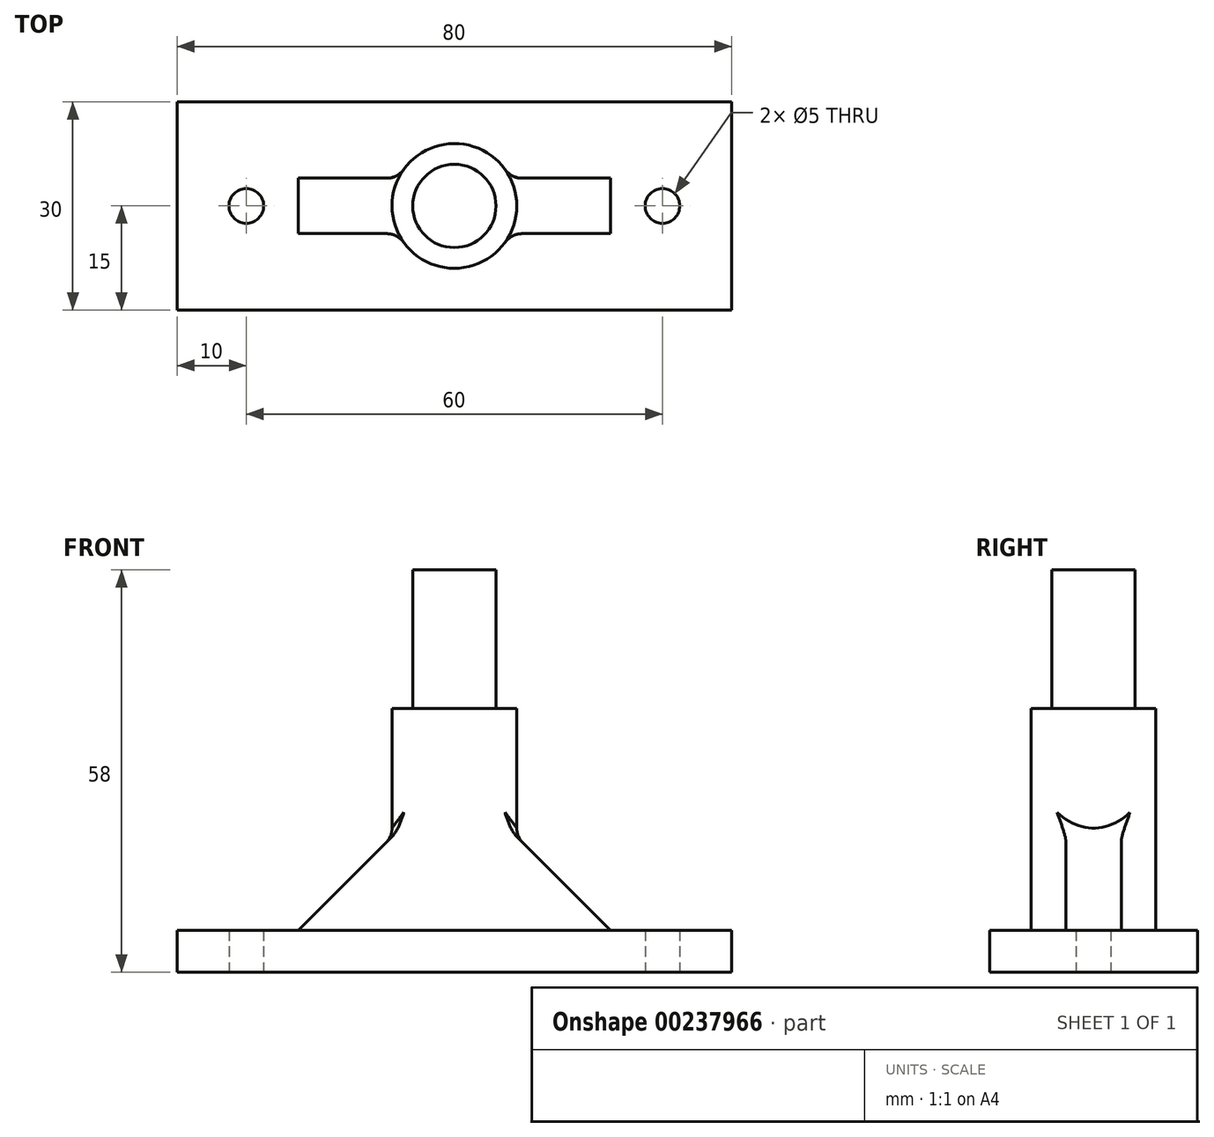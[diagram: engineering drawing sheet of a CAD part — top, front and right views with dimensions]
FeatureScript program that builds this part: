
annotation { "Feature Type Name" : "Feature", "Feature Type Description" : "" }
export const myFeature = defineFeature(function(context is Context, id is Id, definition is map)
    precondition{}
    {
        {
            var Q0;
            Q0=qCreatedBy(makeId("Top.planeOp"),FACE);
            var sketch = newSketch(context, id + "F0", { "sketchPlane" : qUnion([Q0])});
            skLineSegment(sketch, "E0.bottom", {"start": v(-40, 15) * mm, "end": v(40, 15) * mm});
            skLineSegment(sketch, "E0.top", {"start": v(-40, -15) * mm, "end": v(40, -15) * mm});
            skLineSegment(sketch, "E0.left", {"start": v(-40, 15) * mm, "end": v(-40, -15) * mm});
            skLineSegment(sketch, "E0.right", {"start": v(40, 15) * mm, "end": v(40, -15) * mm});
            skCircle(sketch, "E1", {"center": v(-30, 0) * mm, "radius": 2.5 * mm});
            skCircle(sketch, "E2", {"center": v(30, 0) * mm, "radius": 2.5 * mm});
            skSolve(sketch);
        }
        {
            var Q0;
            Q0=makeQuery(id+"F0.imprint","IMPRINT",FACE,{"disambiguationData":[TD([[makeQuery(id+"F0.imprint","IMPRINT",EDGE,{"derivedFrom":sQuery(id+"F0.wireOp",EDGE,"E0.bottom")}),-1.0]])]});
            extrude(context, id + "F1", {"entities" : qUnion([Q0]), "depth" : 6 * mm});
        }
        {
            var Q0;
            Q0=makeQuery(id+"F1.opExtrude","CAP_FACE",FACE,{"disambiguationData":[OSD([sQuery(id+"F0.wireOp",EDGE,"E0.bottom"),sQuery(id+"F0.wireOp",EDGE,"E0.top"),sQuery(id+"F0.wireOp",EDGE,"E0.left"),sQuery(id+"F0.wireOp",EDGE,"E0.right"),sQuery(id+"F0.wireOp",EDGE,"E1"),sQuery(id+"F0.wireOp",EDGE,"E2")])],"isStart":false});
            var sketch = newSketch(context, id + "F2", { "sketchPlane" : qUnion([Q0])});
            skCircle(sketch, "E3", {"center": v(0, 0) * mm, "radius": 9 * mm});
            skSolve(sketch);
        }
        {
            var Q0;
            Q0=makeQuery(id+"F2.imprint","IMPRINT",FACE,{"disambiguationData":[TD([[makeQuery(id+"F2.imprint","IMPRINT",EDGE,{"derivedFrom":sQuery(id+"F2.wireOp",EDGE,"E3")}),1.0]])]});
            extrude(context, id + "F3", {"entities" : qUnion([Q0]), "operationType" : NewBodyOperationType.ADD, "depth" : 32 * mm});
        }
        {
            var Q0;
            Q0=qCreatedBy(makeId("Front.planeOp"),FACE);
            var sketch = newSketch(context, id + "F4", { "sketchPlane" : qUnion([Q0])});
            skLineSegment(sketch, "E4", {"start": v(-7.5, 21) * mm, "end": v(-7.5, 6) * mm});
            skLineSegment(sketch, "E5", {"start": v(-7.5, 6) * mm, "end": v(-22.5, 6) * mm});
            skLineSegment(sketch, "E6", {"start": v(-22.5, 6) * mm, "end": v(-7.5, 21) * mm});
            skLineSegment(sketch, "E7", {"start": v(7.5, 21) * mm, "end": v(22.5, 6) * mm});
            skLineSegment(sketch, "E8", {"start": v(22.5, 6) * mm, "end": v(7.5, 6) * mm});
            skLineSegment(sketch, "E9", {"start": v(7.5, 6) * mm, "end": v(7.5, 21) * mm});
            skSolve(sketch);
        }
        {
            var Q0;
            Q0=makeQuery(id+"F4.imprint","IMPRINT",FACE,{"disambiguationData":[TD([[makeQuery(id+"F4.imprint","IMPRINT",EDGE,{"derivedFrom":sQuery(id+"F4.wireOp",EDGE,"E7")}),-1.0]])]});
            var Q1;
            Q1=makeQuery(id+"F4.imprint","IMPRINT",FACE,{"disambiguationData":[TD([[makeQuery(id+"F4.imprint","IMPRINT",EDGE,{"derivedFrom":sQuery(id+"F4.wireOp",EDGE,"E4")}),-1.0]])]});
            extrude(context, id + "F5", {"entities" : qUnion([Q0, Q1]), "operationType" : NewBodyOperationType.ADD, "endBound" : BoundingType.SYMMETRIC, "depth" : 8 * mm});
        }
        {
            var Q0;
            Q0=makeQuery(id+"F5.boolean.opBoolean","INTERSECT",EDGE,{"derivedFrom":[makeQuery(id+"F3.opExtrude","SWEPT_FACE",FACE,{"disambiguationData":[OSD([sQuery(id+"F2.wireOp",EDGE,"E3")])]}),makeQuery(id+"F5.opExtrude","SWEPT_FACE",FACE,{"disambiguationData":[OSD([sQuery(id+"F4.wireOp",EDGE,"E7")])]})]});
            var Q1;
            Q1=makeQuery(id+"F5.boolean.opBoolean","INTERSECT",EDGE,{"derivedFrom":[makeQuery(id+"F3.opExtrude","SWEPT_FACE",FACE,{"disambiguationData":[OSD([sQuery(id+"F2.wireOp",EDGE,"E3")])]}),makeQuery(id+"F5.opExtrude","SWEPT_FACE",FACE,{"disambiguationData":[OSD([sQuery(id+"F4.wireOp",EDGE,"E6")])]})]});
            var Q2;
            Q2=makeQuery(id+"F5.boolean.opBoolean","INTERSECT",EDGE,{"derivedFrom":[makeQuery(id+"F3.opExtrude","SWEPT_FACE",FACE,{"disambiguationData":[OSD([sQuery(id+"F2.wireOp",EDGE,"E3")])]}),makeQuery(id+"F5.opExtrude","CAP_FACE",FACE,{"disambiguationData":[OSD([sQuery(id+"F4.wireOp",EDGE,"E4"),sQuery(id+"F4.wireOp",EDGE,"E5"),sQuery(id+"F4.wireOp",EDGE,"E6")])],"isStart":false})]});
            var Q3;
            Q3=makeQuery(id+"F5.opExtrude","CAP_EDGE",EDGE,{"disambiguationData":[OSD([sQuery(id+"F4.wireOp",EDGE,"E5")])],"isStart":false});
            var Q4;
            Q4=makeQuery(id+"F5.boolean.opBoolean","INTERSECT",EDGE,{"derivedFrom":[makeQuery(id+"F3.opExtrude","SWEPT_FACE",FACE,{"disambiguationData":[OSD([sQuery(id+"F2.wireOp",EDGE,"E3")])]}),makeQuery(id+"F5.opExtrude","CAP_FACE",FACE,{"disambiguationData":[OSD([sQuery(id+"F4.wireOp",EDGE,"E7"),sQuery(id+"F4.wireOp",EDGE,"E8"),sQuery(id+"F4.wireOp",EDGE,"E9")])],"isStart":false})]});
            var Q5;
            Q5=makeQuery(id+"F5.opExtrude","CAP_EDGE",EDGE,{"disambiguationData":[OSD([sQuery(id+"F4.wireOp",EDGE,"E8")])],"isStart":false});
            var Q6;
            Q6=makeQuery(id+"F5.boolean.opBoolean","INTERSECT",EDGE,{"derivedFrom":[makeQuery(id+"F3.opExtrude","SWEPT_FACE",FACE,{"disambiguationData":[OSD([sQuery(id+"F2.wireOp",EDGE,"E3")])]}),makeQuery(id+"F5.opExtrude","CAP_FACE",FACE,{"disambiguationData":[OSD([sQuery(id+"F4.wireOp",EDGE,"E7"),sQuery(id+"F4.wireOp",EDGE,"E8"),sQuery(id+"F4.wireOp",EDGE,"E9")])],"isStart":true})]});
            var Q7;
            Q7=makeQuery(id+"F5.opExtrude","CAP_EDGE",EDGE,{"disambiguationData":[OSD([sQuery(id+"F4.wireOp",EDGE,"E8")])],"isStart":true});
            var Q8;
            Q8=makeQuery(id+"F5.opExtrude","SWEPT_EDGE",EDGE,{"disambiguationData":[OSD([sQuery(id+"F4.wireOp",EDGE,"E7"),sQuery(id+"F4.wireOp",EDGE,"E8")])]});
            var Q9;
            Q9=makeQuery(id+"F5.boolean.opBoolean","INTERSECT",EDGE,{"derivedFrom":[makeQuery(id+"F3.opExtrude","SWEPT_FACE",FACE,{"disambiguationData":[OSD([sQuery(id+"F2.wireOp",EDGE,"E3")])]}),makeQuery(id+"F5.opExtrude","CAP_FACE",FACE,{"disambiguationData":[OSD([sQuery(id+"F4.wireOp",EDGE,"E4"),sQuery(id+"F4.wireOp",EDGE,"E5"),sQuery(id+"F4.wireOp",EDGE,"E6")])],"isStart":true})]});
            var Q10;
            Q10=makeQuery(id+"F5.opExtrude","CAP_EDGE",EDGE,{"disambiguationData":[OSD([sQuery(id+"F4.wireOp",EDGE,"E5")])],"isStart":true});
            var Q11;
            Q11=makeQuery(id+"F5.opExtrude","SWEPT_EDGE",EDGE,{"disambiguationData":[OSD([sQuery(id+"F4.wireOp",EDGE,"E5"),sQuery(id+"F4.wireOp",EDGE,"E6")])]});
            fillet(context, id + "F6", {"entities" : qUnion([Q0, Q1, Q2, Q3, Q4, Q5, Q6, Q7, Q8, Q9, Q10, Q11]), "radius" : 3 * mm, "tangentPropagation" : true, "allowEdgeOverflow" : false});
        }
        {
            var Q0;
            Q0=makeQuery(id+"F3.opExtrude","CAP_FACE",FACE,{"disambiguationData":[OSD([sQuery(id+"F2.wireOp",EDGE,"E3")])],"isStart":false});
            var sketch = newSketch(context, id + "F7", { "sketchPlane" : qUnion([Q0])});
            skCircle(sketch, "E10", {"center": v(0, 0) * mm, "radius": 6 * mm});
            skSolve(sketch);
        }
        {
            var Q0;
            Q0=makeQuery(id+"F7.imprint","IMPRINT",FACE,{"disambiguationData":[TD([[makeQuery(id+"F7.imprint","IMPRINT",EDGE,{"derivedFrom":sQuery(id+"F7.wireOp",EDGE,"E10")}),1.0]])]});
            extrude(context, id + "F8", {"entities" : qUnion([Q0]), "operationType" : NewBodyOperationType.ADD, "depth" : 20 * mm});
        }
    });
